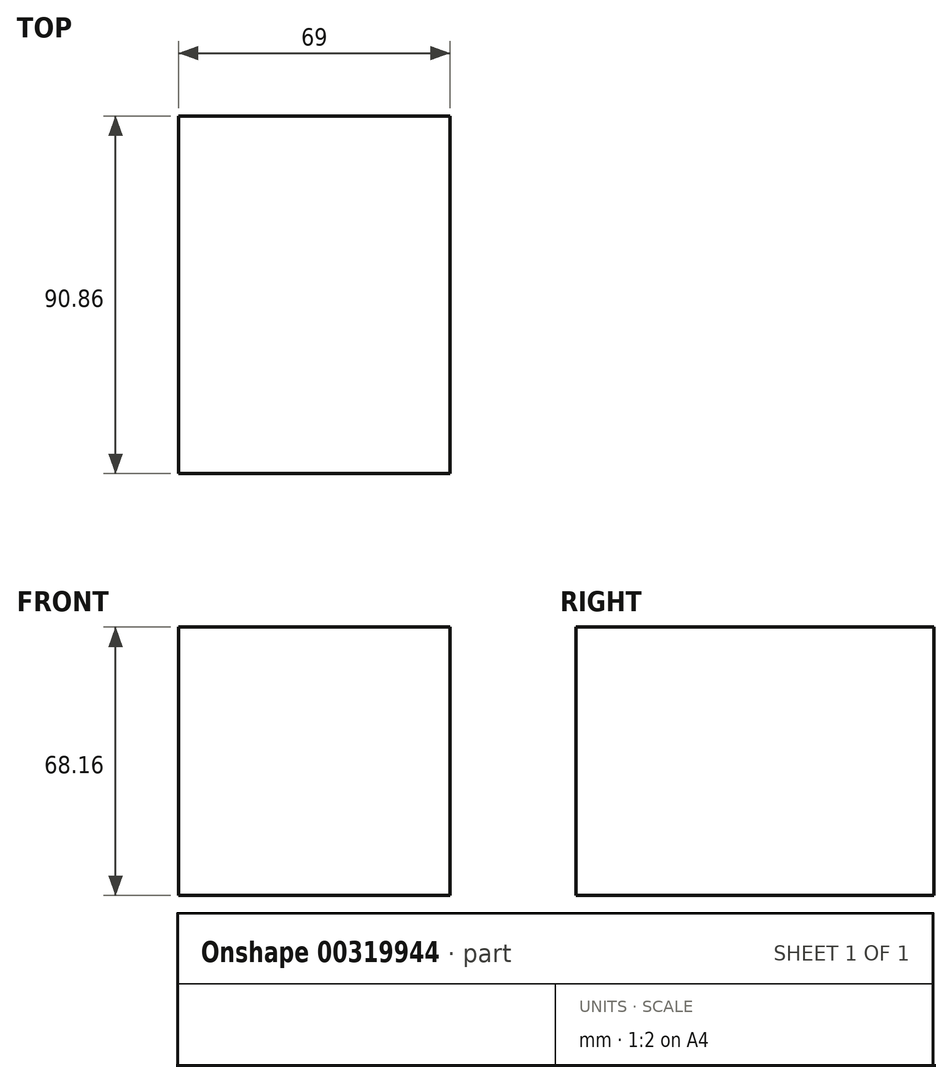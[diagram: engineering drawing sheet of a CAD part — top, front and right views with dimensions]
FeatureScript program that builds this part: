
annotation { "Feature Type Name" : "Feature", "Feature Type Description" : "" }
export const myFeature = defineFeature(function(context is Context, id is Id, definition is map)
    precondition{}
    {
        {
            var Q0;
            Q0=qCreatedBy(makeId("Top.planeOp"),FACE);
            var sketch = newSketch(context, id + "F0", { "sketchPlane" : qUnion([Q0])});
            skLineSegment(sketch, "E0.bottom", {"start": v(11.18, 12.29) * mm, "end": v(80.18, 12.29) * mm});
            skLineSegment(sketch, "E0.top", {"start": v(11.18, 103.15) * mm, "end": v(80.18, 103.15) * mm});
            skLineSegment(sketch, "E0.left", {"start": v(11.18, 12.29) * mm, "end": v(11.18, 103.15) * mm});
            skLineSegment(sketch, "E0.right", {"start": v(80.18, 12.29) * mm, "end": v(80.18, 103.15) * mm});
            skSolve(sketch);
        }
        {
            var Q0;
            Q0=makeQuery(id+"F0.imprint","IMPRINT",FACE,{"disambiguationData":[TD([[makeQuery(id+"F0.imprint","IMPRINT",EDGE,{"derivedFrom":sQuery(id+"F0.wireOp",EDGE,"E0.bottom")}),1.0]])]});
            extrude(context, id + "F1", {"entities" : qUnion([Q0]), "depth" : 68.16 * mm});
        }
    });
